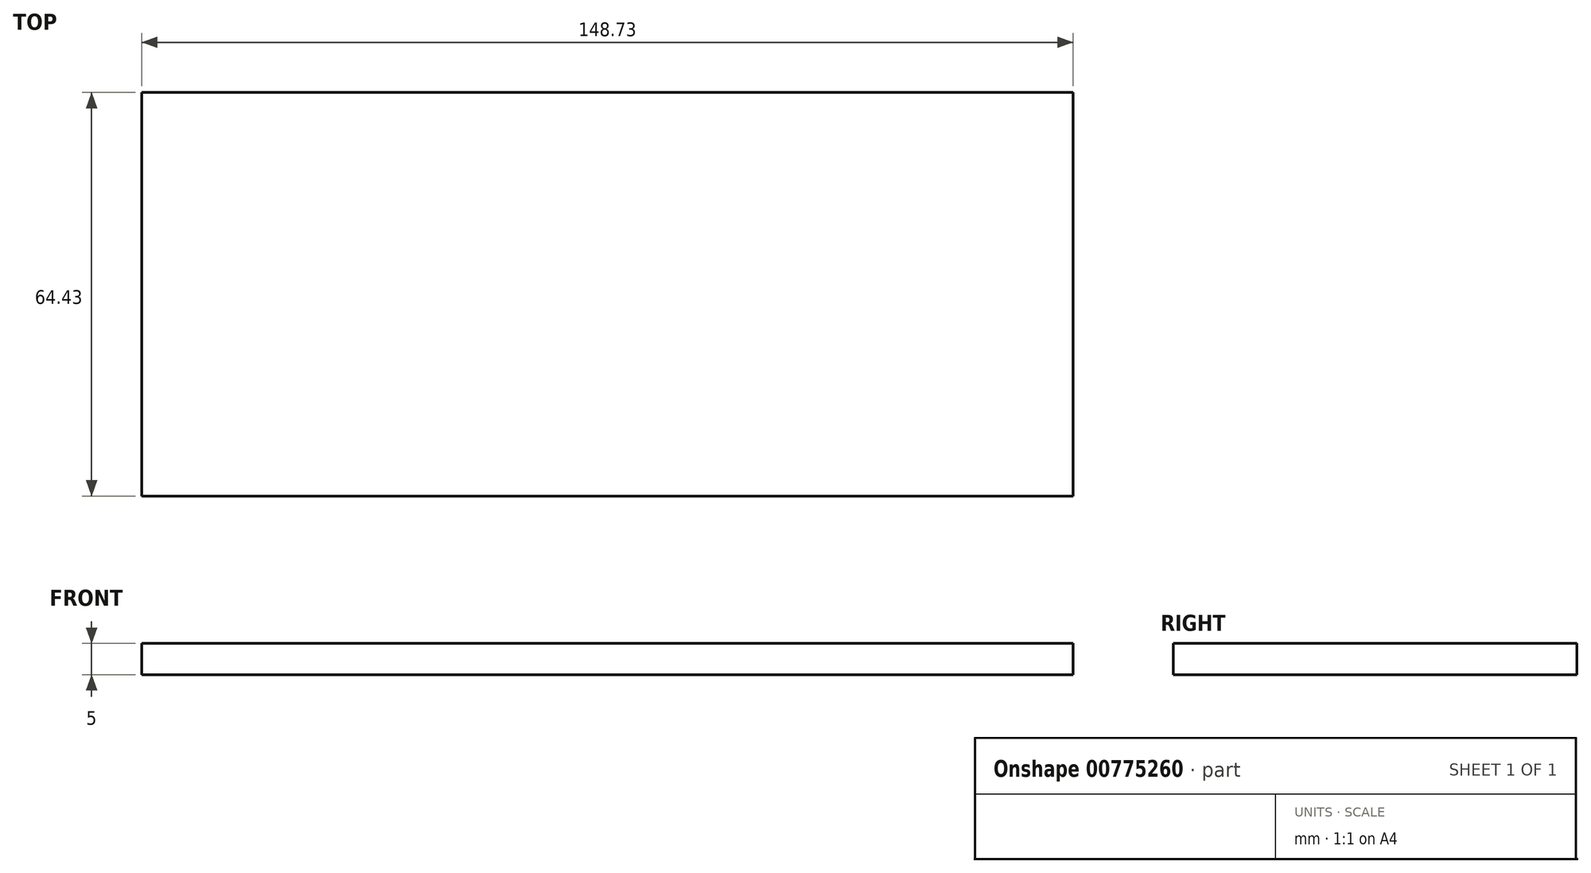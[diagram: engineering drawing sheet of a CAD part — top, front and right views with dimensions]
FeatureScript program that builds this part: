
annotation { "Feature Type Name" : "Feature", "Feature Type Description" : "" }
export const myFeature = defineFeature(function(context is Context, id is Id, definition is map)
    precondition{}
    {
        {
            var Q0;
            Q0=qCreatedBy(makeId("Top.planeOp"),FACE);
            var sketch = newSketch(context, id + "F0", { "sketchPlane" : qUnion([Q0])});
            skLineSegment(sketch, "E0.bottom", {"start": v(-74.06, -31.3) * mm, "end": v(74.67, -31.3) * mm});
            skLineSegment(sketch, "E0.top", {"start": v(-74.06, 33.13) * mm, "end": v(74.67, 33.13) * mm});
            skLineSegment(sketch, "E0.left", {"start": v(-74.06, -31.3) * mm, "end": v(-74.06, 33.13) * mm});
            skLineSegment(sketch, "E0.right", {"start": v(74.67, -31.3) * mm, "end": v(74.67, 33.13) * mm});
            skSolve(sketch);
        }
        {
            var Q0;
            Q0=makeQuery(id+"F0.imprint","IMPRINT",FACE,{"disambiguationData":[TD([[makeQuery(id+"F0.imprint","IMPRINT",EDGE,{"derivedFrom":sQuery(id+"F0.wireOp",EDGE,"E0.bottom")}),1.0]])]});
            extrude(context, id + "F1", {"entities" : qUnion([Q0]), "depth" : 5 * mm, "offsetDistance" : 25 * mm});
        }
    });
